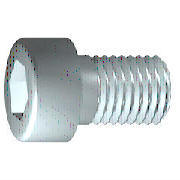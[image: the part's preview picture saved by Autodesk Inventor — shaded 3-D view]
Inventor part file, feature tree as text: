
AUTODESK INVENTOR PART (.ipt)
format: ipt  version: 2013 (Build 170138000, 138)  size: 187,904 bytes
history: native  units: mm (DEFAULTED — no unit token found)
features: sketch x2, extrude x1, plane x1, fillet x1
ambient origin geometry x7: Origin, YZ Plane, XY Plane, X Axis, Y Axis, Z Axis, Center Point
bodies: Solid1 (feature_tree), Body (feature_tree)
feature tree (5):
  extrude  "Slot"  Depth=0.429515mm
  plane  "Work Plane1"
  fillet  "Fillet2"  Radius=4.0mm
  sketch  "Sketch1"  dims[d1=14.25mm d2=0.429515mm d3=4.0mm]
  sketch  "Sketch2"  dims[d4=2.0mm d5=60.0deg d6=4.0mm d7=4.0mm d8=3.464102mm d9=7.0mm d10=90.0deg d11=10.0mm d12=0.0mm d13=14.25mm d14=0.0mm d15=0.429415mm d16=0.429415mm d17=0.4mm d19=0.0mm d26=16.0mm d27=45.0deg d28=0.0mm d29=0.0mm d30=0.1mm]
